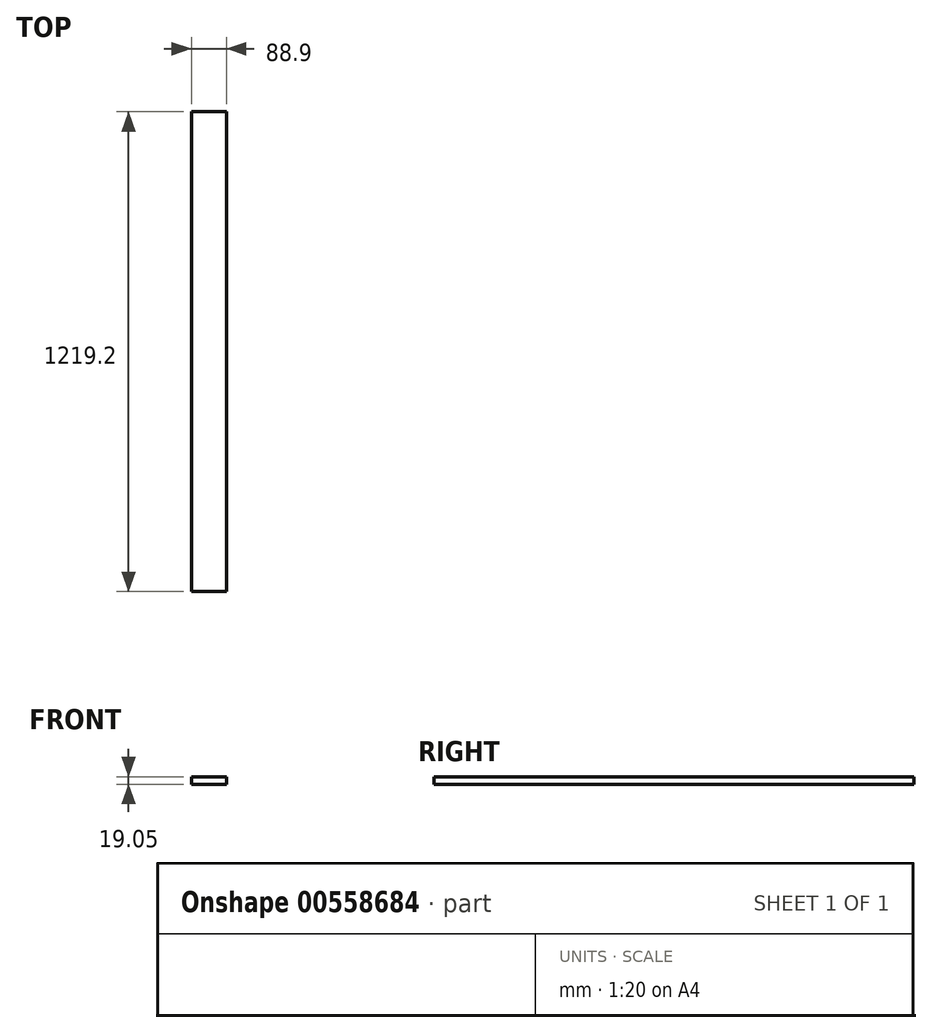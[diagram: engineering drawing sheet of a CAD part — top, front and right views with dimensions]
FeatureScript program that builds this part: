
annotation { "Feature Type Name" : "Feature", "Feature Type Description" : "" }
export const myFeature = defineFeature(function(context is Context, id is Id, definition is map)
    precondition{}
    {
        {
            var Q0;
            Q0=qCreatedBy(makeId("Top.planeOp"),FACE);
            var sketch = newSketch(context, id + "F0", { "sketchPlane" : qUnion([Q0])});
            skLineSegment(sketch, "E0.bottom", {"start": v(-202.7, -630.37) * mm, "end": v(-113.8, -630.37) * mm});
            skLineSegment(sketch, "E0.top", {"start": v(-202.7, 588.83) * mm, "end": v(-113.8, 588.83) * mm});
            skLineSegment(sketch, "E0.left", {"start": v(-202.7, -630.37) * mm, "end": v(-202.7, 588.83) * mm});
            skLineSegment(sketch, "E0.right", {"start": v(-113.8, -630.37) * mm, "end": v(-113.8, 588.83) * mm});
            skSolve(sketch);
        }
        {
            var Q0;
            Q0=makeQuery(id+"F0.imprint","IMPRINT",FACE,{"disambiguationData":[TD([[makeQuery(id+"F0.imprint","IMPRINT",EDGE,{"derivedFrom":sQuery(id+"F0.wireOp",EDGE,"E0.bottom")}),1.0]])]});
            extrude(context, id + "F1", {"entities" : qUnion([Q0]), "depth" : 19.05 * mm, "offsetDistance" : 25.4 * mm});
        }
    });
